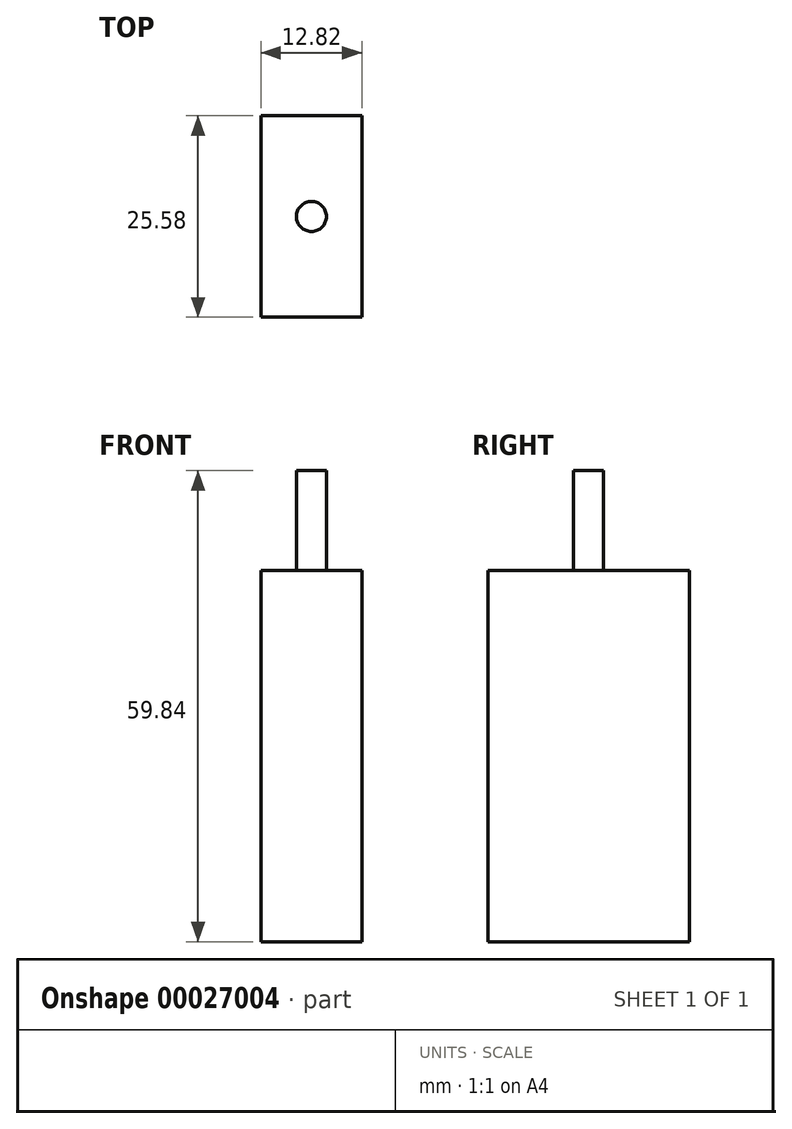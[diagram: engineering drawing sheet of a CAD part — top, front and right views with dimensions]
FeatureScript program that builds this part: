
annotation { "Feature Type Name" : "Feature", "Feature Type Description" : "" }
export const myFeature = defineFeature(function(context is Context, id is Id, definition is map)
    precondition{}
    {
        {
            var Q0;
            Q0=qCreatedBy(makeId("Top.planeOp"),FACE);
            var sketch = newSketch(context, id + "F0", { "sketchPlane" : qUnion([Q0])});
            skLineSegment(sketch, "E0.rect.bottom", {"start": v(6.41, -12.8) * mm, "end": v(-6.41, -12.8) * mm});
            skLineSegment(sketch, "E0.rect.top", {"start": v(6.41, 12.8) * mm, "end": v(-6.41, 12.8) * mm});
            skLineSegment(sketch, "E0.rect.left", {"start": v(6.41, -12.8) * mm, "end": v(6.41, 12.8) * mm});
            skLineSegment(sketch, "E0.rect.right", {"start": v(-6.41, -12.8) * mm, "end": v(-6.41, 12.8) * mm});
            skPoint(sketch, "E0.rect.middle", {"position": v(0, 0) * mm});
            skSolve(sketch);
        }
        {
            var Q0;
            Q0 = qSketchRegion(id + "F0", true);
            extrude(context, id + "F1", {"entities" : qUnion([Q0]), "depth" : 47.14 * mm});
        }
        {
            var Q0;
            Q0=makeQuery(id+"F1.opExtrude","CAP_FACE",FACE,{"disambiguationData":[OSD([sQuery(id+"F0.wireOp",EDGE,"E0.rect.bottom"),sQuery(id+"F0.wireOp",EDGE,"E0.rect.top"),sQuery(id+"F0.wireOp",EDGE,"E0.rect.left"),sQuery(id+"F0.wireOp",EDGE,"E0.rect.right")])],"isStart":false});
            var sketch = newSketch(context, id + "F2", { "sketchPlane" : qUnion([Q0])});
            skCircle(sketch, "E1", {"center": v(0, 0) * mm, "radius": 1.9 * mm});
            skSolve(sketch);
        }
        {
            var Q0;
            Q0=makeQuery(id+"F2.imprint","IMPRINT",FACE,{"disambiguationData":[TD([[makeQuery(id+"F2.imprint","IMPRINT",EDGE,{"derivedFrom":sQuery(id+"F2.wireOp",EDGE,"E1")}),1.0]])]});
            extrude(context, id + "F3", {"entities" : qUnion([Q0]), "operationType" : NewBodyOperationType.ADD, "depth" : 12.7 * mm});
        }
    });
